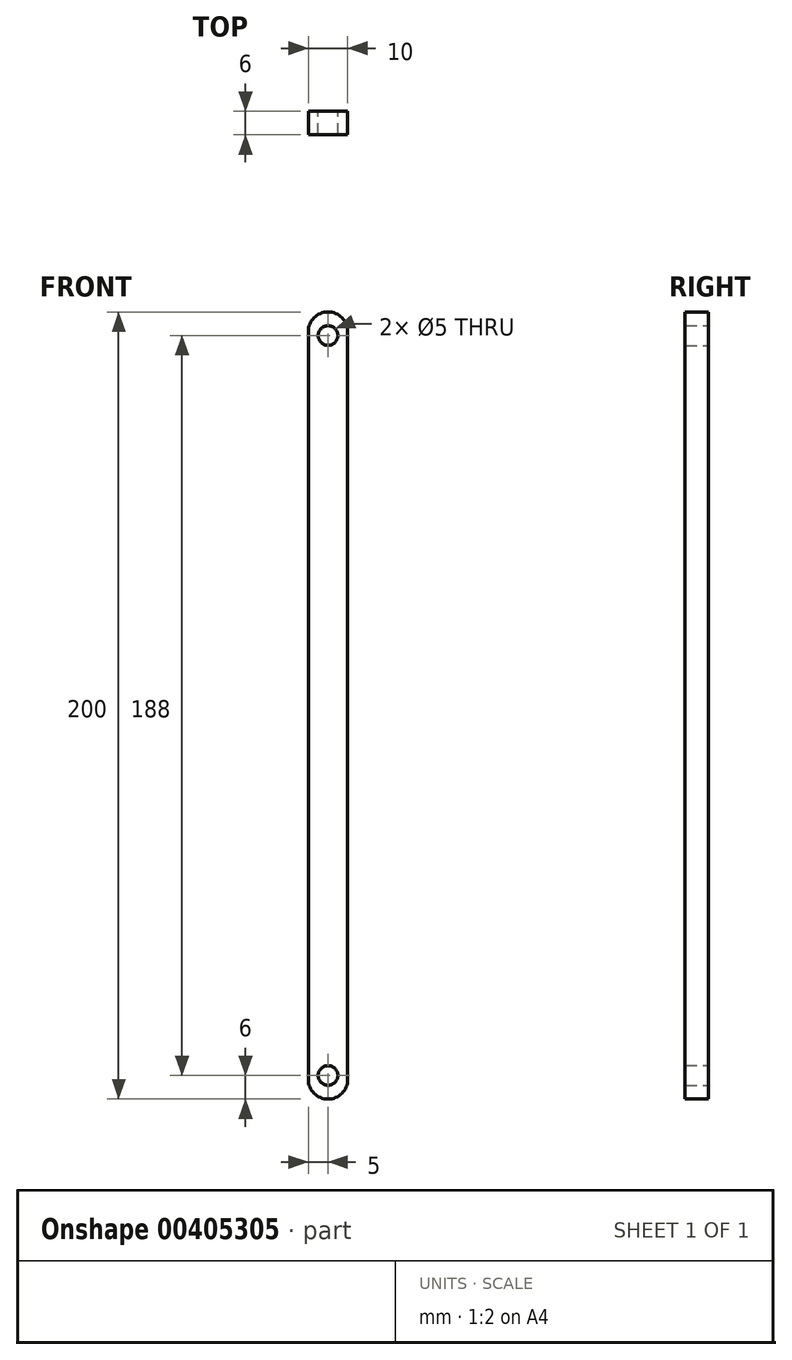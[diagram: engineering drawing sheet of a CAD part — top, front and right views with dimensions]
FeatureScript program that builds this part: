
annotation { "Feature Type Name" : "Feature", "Feature Type Description" : "" }
export const myFeature = defineFeature(function(context is Context, id is Id, definition is map)
    precondition{}
    {
        {
            var Q0;
            Q0=qCreatedBy(makeId("Front.planeOp"),FACE);
            var sketch = newSketch(context, id + "F0", { "sketchPlane" : qUnion([Q0])});
            skLineSegment(sketch, "E0.bottom", {"start": v(-5, -100) * mm, "end": v(5, -100) * mm});
            skLineSegment(sketch, "E0.top", {"start": v(-5, 100) * mm, "end": v(5, 100) * mm});
            skLineSegment(sketch, "E0.left", {"start": v(-5, -100) * mm, "end": v(-5, 100) * mm});
            skLineSegment(sketch, "E0.right", {"start": v(5, -100) * mm, "end": v(5, 100) * mm});
            skPoint(sketch, "E0.middle", {"position": v(0, 0) * mm});
            skCircle(sketch, "E1", {"center": v(0, 94) * mm, "radius": 2.5 * mm});
            skCircle(sketch, "E2", {"center": v(0, -94) * mm, "radius": 2.5 * mm});
            skPoint(sketch, "E2.centerSnap0", {"position": v(0, -100) * mm});
            skSolve(sketch);
        }
        {
            var Q0;
            Q0=makeQuery(id+"F0.imprint","IMPRINT",FACE,{"disambiguationData":[TD([[makeQuery(id+"F0.imprint","IMPRINT",EDGE,{"derivedFrom":sQuery(id+"F0.wireOp",EDGE,"E0.bottom")}),1.0]])]});
            extrude(context, id + "F1", {"entities" : qUnion([Q0]), "depth" : 6 * mm});
        }
        {
            var Q0;
            Q0=makeQuery(id+"F1.opExtrude","SWEPT_EDGE",EDGE,{"disambiguationData":[OSD([sQuery(id+"F0.wireOp",EDGE,"E0.top"),sQuery(id+"F0.wireOp",EDGE,"E0.left")])]});
            var Q1;
            Q1=makeQuery(id+"F1.opExtrude","SWEPT_EDGE",EDGE,{"disambiguationData":[OSD([sQuery(id+"F0.wireOp",EDGE,"E0.top"),sQuery(id+"F0.wireOp",EDGE,"E0.right")])]});
            var Q2;
            Q2=makeQuery(id+"F1.opExtrude","SWEPT_EDGE",EDGE,{"disambiguationData":[OSD([sQuery(id+"F0.wireOp",EDGE,"E0.bottom"),sQuery(id+"F0.wireOp",EDGE,"E0.right")])]});
            var Q3;
            Q3=makeQuery(id+"F1.opExtrude","SWEPT_EDGE",EDGE,{"disambiguationData":[OSD([sQuery(id+"F0.wireOp",EDGE,"E0.bottom"),sQuery(id+"F0.wireOp",EDGE,"E0.left")])]});
            fillet(context, id + "F2", {"entities" : qUnion([Q0, Q1, Q2, Q3]), "radius" : 5 * mm, "tangentPropagation" : true, "allowEdgeOverflow" : false});
        }
    });
